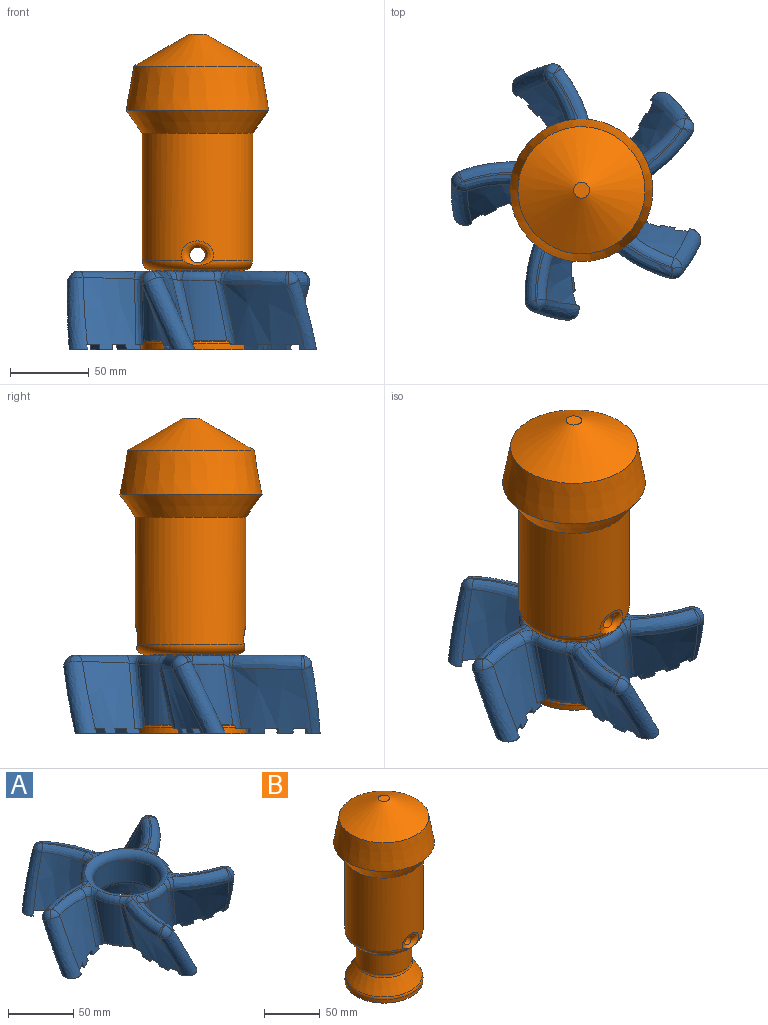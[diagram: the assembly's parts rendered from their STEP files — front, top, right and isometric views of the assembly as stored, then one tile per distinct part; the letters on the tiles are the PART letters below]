
ASSEMBLY  parts=2 mates=1
PART A: 225 faces, bbox 175.2x182.1x61 mm
  f0: plane 42.35x20.28mm, normal (0,0,1), area 71.8mm2, adj f1,f2,f3,f4,f5,f6,f7
  f1: bspline ~10.62x7.36mm, area 56.3mm2, adj f0,f2,f8,f9
  f2: bspline ~43.17x22.23mm, area 274.2mm2, adj f0,f1,f3,f10
  f3: bspline ~8.45x6.28mm, area 40.2mm2, adj f0,f2,f11,f12
  f4: bspline ~9.09x8.11mm, area 21.1mm2, adj f0,f5,f11,f12
  f5: bspline ~56.02x27.79mm, area 540.1mm2, adj f0,f4,f6,f13
  f6: bspline ~8.4x7.98mm, area 34.4mm2, adj f0,f5,f14,f15
  f7: torus R=31.68mm, axis (0,0,-1), area 1732.1mm2, adj f0,f8,f14,f16,f17,f18,f19,f20
  f8: bspline ~9.22x6.2mm, area 33.1mm2, adj f1,f7,f9,f31
  f9: bspline ~52.96x14.35mm, area 308.9mm2, adj f1,f8,f10,f34,f35,f36,f37
  f10: bspline ~61.21x58.82mm, area 1531.5mm2, adj f2,f9,f12,f36,f38,f39,f40,f41
  f11: bspline ~9.17x8.69mm, area 43.6mm2, adj f3,f4,f12
  f12: bspline ~58.82x48.97mm, area 1090.9mm2, adj f3,f4,f10,f11,f13,f38,f46,f47
  f13: bspline ~69.73x58.82mm, area 1849.8mm2, adj f5,f12,f15,f36,f38,f39,f41,f42
  f14: bspline ~9.32x7.99mm, area 39.3mm2, adj f6,f7,f15,f30
  f15: bspline ~52.82x15.4mm, area 214.3mm2, adj f6,f13,f14,f34,f35,f36,f53
  f16: cylinder r=25.33mm len=50.66mm, axis (0,0,-1), area 3136mm2, adj f7,f54
  f17: bspline ~8.62x6.2mm, area 33.1mm2, adj f7,f18,f55,f56
  f18: torus R=28.5mm, axis (0,0,1), area 139.8mm2, adj f7,f17,f19,f57
  f19: bspline ~8.7x7.99mm, area 39.3mm2, adj f7,f18,f58,f59
  f20: plane 45.94x13.84mm, normal (0,0,1), area 71.8mm2, adj f7,f58,f60,f61,f62,f63,f64
  f21: bspline ~8.02x6.42mm, area 33.1mm2, adj f7,f22,f60,f65
  f22: torus R=28.5mm, axis (0,0,1), area 139.8mm2, adj f7,f21,f23,f66
  f23: bspline ~7.99x7.98mm, area 39.3mm2, adj f7,f22,f67,f68
  f24: plane 41.07x26.12mm, normal (0,0,1), area 71.8mm2, adj f7,f68,f69,f70,f71,f72,f73
  f25: bspline ~8.18x6.64mm, area 33.1mm2, adj f7,f26,f72,f74
  f26: torus R=28.5mm, axis (0,0,1), area 139.8mm2, adj f7,f25,f27,f75
  f27: bspline ~8.67x7.99mm, area 39.3mm2, adj f7,f26,f76,f77
  f28: plane 35.99x32.2mm, normal (0,0,1), area 71.8mm2, adj f7,f77,f78,f79,f80,f81,f82
  f29: bspline ~9.15x6.44mm, area 33.1mm2, adj f7,f30,f81,f83
  f30: torus R=28.5mm, axis (0,0,1), area 139.8mm2, adj f7,f14,f29,f53
  f31: torus R=28.5mm, axis (0,0,1), area 139.8mm2, adj f7,f8,f32,f37
  f32: bspline ~9.1x7.81mm, area 39.3mm2, adj f7,f31,f84,f85
  f33: plane 46.31x6.53mm, normal (0,0,1), area 71.8mm2, adj f7,f55,f84,f86,f87,f88,f89
  f34: torus R=30.33mm, axis (0,0,-1), area 364.3mm2, adj f9,f15,f35,f37,f53,f56,f57,f59
  f35: cylinder r=35.33mm len=18.77mm, axis (0,0,-1), area 1.8mm2, adj f9,f15,f34,f36
  f36: plane 18.75x12.96mm, normal (0,0,-1), area 72.9mm2, adj f9,f10,f13,f15,f35,f45
  f37: cylinder r=35mm len=38.6mm, axis (0,0,-1), area 809.9mm2, adj f9,f31,f34,f85
  f38: plane 18.21x15.93mm, normal (0,0,-1), area 134.9mm2, adj f10,f12,f13,f39,f49
  f39: plane 12.49x10.79mm, normal (-0.65,0.76,0), area 55.7mm2, adj f10,f13,f38,f51,f95,f96,f97
  f40: plane 6.58x6.34mm, normal (0,0,1), area 0mm2, adj f10,f97
  f41: plane 12.32x10.63mm, normal (0.65,-0.76,0), area 55.5mm2, adj f10,f13,f42,f51,f95,f96,f97
  f42: plane 17.06x16.85mm, normal (0,0,-1), area 135.3mm2, adj f10,f13,f41,f43
  f43: plane 12.25x10.57mm, normal (-0.65,0.76,0), area 55.8mm2, adj f10,f13,f42,f50,f98,f99,f100
  f44: plane 7.76x4.83mm, normal (0,0,1), area 0mm2, adj f10,f100
  f45: plane 12.29x10.61mm, normal (0.65,-0.76,0), area 56.6mm2, adj f10,f13,f36,f50,f98,f99,f100
  f46: cylinder r=7.5mm len=8.2mm, axis (0,0,-1), area 0.9mm2, adj f12,f52,f101,f102
  f47: cylinder r=7.5mm len=12.48mm, axis (0,0,-1), area 0mm2, adj f12,f48,f49,f102
  f48: plane 12.66x4.02mm, normal (0,0,-1), area 0mm2, adj f12,f47
  f49: plane 12.78x11.04mm, normal (0.65,-0.76,0), area 56.4mm2, adj f12,f13,f38,f47,f52,f101,f102
  f50: cylinder r=100.66mm len=7.6mm, axis (0,0,-1), area 0.9mm2, adj f13,f43,f45,f98
  f51: cylinder r=100.66mm len=6.59mm, axis (0,0,-1), area 0.9mm2, adj f13,f39,f41,f95
  f52: cylinder r=100.66mm len=2.48mm, axis (0,0,-1), area 0.3mm2, adj f13,f46,f49,f101
  f53: cylinder r=35mm len=38.6mm, axis (0,0,-1), area 809.9mm2, adj f15,f30,f34,f83
  f54: torus R=30.33mm, axis (0,0,-1), area 420.4mm2, adj f16,f91
  f55: bspline ~8.93x8.44mm, area 56.3mm2, adj f17,f33,f56,f86
  f56: bspline ~52.96x16.05mm, area 308.9mm2, adj f17,f34,f55,f57,f90,f103,f104
  f57: cylinder r=35mm len=38.6mm, axis (0,0,-1), area 809.9mm2, adj f18,f34,f56,f59
  f58: bspline ~8.62x7.98mm, area 34.4mm2, adj f19,f20,f59,f64
  f59: bspline ~52.82x12.84mm, area 214.3mm2, adj f19,f34,f57,f58,f92,f105,f106
  f60: bspline ~9.43x9.43mm, area 56.3mm2, adj f20,f21,f61,f65
  f61: bspline ~44.92x16.4mm, area 274.2mm2, adj f20,f60,f62,f107
  f62: bspline ~7.22x6.78mm, area 40.2mm2, adj f20,f61,f108,f109
  f63: bspline ~9.07x6.55mm, area 21.1mm2, adj f20,f64,f108,f109
  f64: bspline ~56.54x22.87mm, area 540.1mm2, adj f20,f58,f63,f106
  f65: bspline ~52.96x17.22mm, area 308.9mm2, adj f21,f34,f60,f66,f92,f105,f107
  f66: cylinder r=35mm len=38.6mm, axis (0,0,-1), area 809.9mm2, adj f22,f34,f65,f67
  f67: bspline ~52.82x15.21mm, area 214.3mm2, adj f23,f34,f66,f68,f93,f110,f111
  f68: bspline ~8.97x7.98mm, area 34.4mm2, adj f23,f24,f67,f71
  f69: bspline ~7.29x6.91mm, area 40.2mm2, adj f24,f73,f112,f113
  f70: bspline ~9.07x6.55mm, area 21.1mm2, adj f24,f71,f112,f113
  f71: bspline ~51.4x37.99mm, area 540.1mm2, adj f24,f68,f70,f111
  f72: bspline ~9.51x8.59mm, area 56.3mm2, adj f24,f25,f73,f74
  f73: bspline ~41.2x28.55mm, area 274.2mm2, adj f24,f69,f72,f114
  f74: bspline ~52.96x16.7mm, area 308.9mm2, adj f25,f34,f72,f75,f93,f110,f114
  f75: cylinder r=35mm len=38.6mm, axis (0,0,-1), area 809.9mm2, adj f26,f34,f74,f76
  f76: bspline ~52.82x16.09mm, area 214.3mm2, adj f27,f34,f75,f77,f94,f115,f116
  f77: bspline ~8.49x8.43mm, area 34.4mm2, adj f27,f28,f76,f80
  f78: bspline ~7.83x6.78mm, area 40.2mm2, adj f28,f82,f117,f118
  f79: bspline ~9.07x6.39mm, area 21.1mm2, adj f28,f80,f117,f118
  f80: bspline ~49.43x41.63mm, area 540.1mm2, adj f28,f77,f79,f116
  f81: bspline ~9.75x7.17mm, area 56.3mm2, adj f28,f29,f82,f83
  f82: bspline ~31.37x29.68mm, area 274.2mm2, adj f28,f78,f81,f119
  f83: bspline ~52.96x14.55mm, area 308.9mm2, adj f29,f34,f53,f81,f94,f115,f119
  f84: bspline ~8.24x7.98mm, area 34.4mm2, adj f32,f33,f85,f89
  f85: bspline ~52.82x13.2mm, area 214.3mm2, adj f32,f34,f37,f84,f90,f103,f120
  f86: bspline ~46.04x10.7mm, area 274.2mm2, adj f33,f55,f87,f104
  f87: bspline ~8.23x6.31mm, area 40.2mm2, adj f33,f86,f121,f122
  f88: bspline ~9.47x9.09mm, area 21.1mm2, adj f33,f89,f121,f122
  f89: bspline ~58.82x14.67mm, area 540.1mm2, adj f33,f84,f88,f120
  f90: cylinder r=35.33mm len=19.52mm, axis (0,0,-1), area 1.8mm2, adj f34,f56,f85,f103
  f91: cone r=34.66mm half-angle=30deg, axis (0,0,-1), area 3300.8mm2, adj f34,f54
  f92: cylinder r=35.33mm len=18.35mm, axis (0,0,-1), area 1.8mm2, adj f34,f59,f65,f105
  f93: cylinder r=35.33mm len=15.39mm, axis (0,0,-1), area 1.8mm2, adj f34,f67,f74,f110
  f94: cylinder r=35.33mm len=16.19mm, axis (0,0,-1), area 1.8mm2, adj f34,f76,f83,f115
  f95: plane 17.71x16.43mm, normal (0,0,-1), area 136.6mm2, adj f39,f41,f51,f96
  f96: bspline ~56.9x34.03mm, area 1mm2, adj f39,f41,f95,f97
  f97: cylinder r=85.66mm len=6.54mm, axis (0,0,-1), area 0mm2, adj f39,f40,f41,f96
  f98: plane 17.6x16.4mm, normal (0,0,-1), area 136.7mm2, adj f43,f45,f50,f99
  f99: bspline ~56.9x34.03mm, area 0.9mm2, adj f43,f45,f98,f100
  f100: cylinder r=85.66mm len=7.74mm, axis (0,0,-1), area 0mm2, adj f43,f44,f45,f99
  f101: plane 14.53x13.46mm, normal (0,0,-1), area 111.7mm2, adj f46,f49,f52,f102
  f102: bspline ~34.67x29.41mm, area 1.6mm2, adj f46,f47,f49,f101
  f103: plane 19.5x8.87mm, normal (0,0,-1), area 72.9mm2, adj f56,f85,f90,f104,f120,f123
  f104: bspline ~61.2x58.82mm, area 1531.5mm2, adj f56,f86,f103,f122,f123,f124,f125,f126
  f105: plane 18.34x10.86mm, normal (0,0,-1), area 57.6mm2, adj f59,f65,f92,f106,f107,f131
  f106: bspline ~75.44x58.82mm, area 1851.2mm2, adj f59,f64,f105,f109,f131,f132,f133,f134
  f107: bspline ~59.81x58.82mm, area 1532.7mm2, adj f61,f65,f105,f109,f131,f132,f133,f135
  f108: bspline ~8.9x8.69mm, area 65.3mm2, adj f62,f63,f109
  f109: bspline ~58.82x46.45mm, area 1090.9mm2, adj f62,f63,f106,f107,f108,f147,f148,f149
  f110: plane 18.33x14.91mm, normal (0,0,-1), area 72.9mm2, adj f67,f74,f93,f111,f114,f156
  f111: bspline ~70.76x58.82mm, area 1849.8mm2, adj f67,f71,f110,f113,f156,f157,f158,f159
  f112: bspline ~8.69x7.43mm, area 47mm2, adj f69,f70,f113
  f113: bspline ~58.82x42.6mm, area 1090.9mm2, adj f69,f70,f111,f112,f114,f163,f164,f166
  f114: bspline ~58.82x57.24mm, area 1531.5mm2, adj f73,f74,f110,f113,f156,f158,f159,f160
  f115: plane 17.51x16.45mm, normal (0,0,-1), area 72.9mm2, adj f76,f83,f94,f116,f119,f171
  f116: bspline ~62.06x59.15mm, area 1849.8mm2, adj f76,f80,f115,f118,f171,f172,f173,f174
  f117: bspline ~8.69x7.94mm, area 42.7mm2, adj f78,f79,f118
  f118: bspline ~58.82x43.56mm, area 1090.9mm2, adj f78,f79,f116,f117,f119,f178,f179,f181
  f119: bspline ~58.82x55.76mm, area 1531.5mm2, adj f82,f83,f115,f118,f171,f173,f174,f175
  f120: bspline ~73.54x58.82mm, area 1849.8mm2, adj f85,f89,f103,f122,f123,f124,f125,f127
  f121: bspline ~9.5x8.69mm, area 52.2mm2, adj f87,f88,f122
  f122: bspline ~58.82x49.59mm, area 1090.9mm2, adj f87,f88,f104,f120,f121,f124,f188,f190
  f123: plane 14.96x6.29mm, normal (0.92,0.39,0), area 56.6mm2, adj f103,f104,f120,f186,f193,f194,f195
  f124: plane 18.53x13.68mm, normal (0,0,-1), area 134.9mm2, adj f104,f120,f122,f125,f188
  f125: plane 15.21x6.4mm, normal (-0.92,-0.39,0), area 55.7mm2, adj f104,f120,f124,f187,f196,f197,f198
  f126: plane 8.2x4.02mm, normal (0,0,1), area 0mm2, adj f104,f198
  f127: plane 15x6.31mm, normal (0.92,0.39,0), area 55.5mm2, adj f104,f120,f128,f187,f196,f197,f198
  f128: plane 16.84x14.38mm, normal (0,0,-1), area 135.3mm2, adj f104,f120,f127,f129
  f129: plane 14.91x6.27mm, normal (-0.92,-0.39,0), area 55.8mm2, adj f104,f120,f128,f186,f193,f194,f195
  f130: plane 8.87x2.21mm, normal (0,0,1), area 0mm2, adj f104,f193
  f131: cylinder r=1mm len=15.41mm, axis (-1,-0.08,0), area 24.1mm2, adj f105,f106,f107,f132
  f132: plane 15.68x1.7mm, normal (-0.08,1,0), area 26mm2, adj f106,f107,f131,f133
  f133: cylinder r=1mm len=15.43mm, axis (-1,-0.08,0), area 24mm2, adj f106,f107,f132,f134,f199,f200,f201
  f134: cylinder r=100.66mm len=7.93mm, axis (0,0,-1), area 0.7mm2, adj f106,f133,f135,f201
  f135: cylinder r=1mm len=15.5mm, axis (1,0.08,0), area 23.7mm2, adj f106,f107,f134,f136,f199,f200,f201
  f136: plane 15.53x1.7mm, normal (0.08,-1,0), area 25.6mm2, adj f106,f107,f135,f137
  f137: cylinder r=1mm len=15.52mm, axis (1,0.08,0), area 23.7mm2, adj f106,f107,f136,f138
  f138: plane 15.14x8.29mm, normal (0,0,-1), area 105.2mm2, adj f106,f107,f137,f139
  f139: cylinder r=1mm len=15.35mm, axis (-1,-0.08,0), area 23.6mm2, adj f106,f107,f138,f140
  f140: plane 15.53x1.7mm, normal (-0.08,1,0), area 25.5mm2, adj f106,f107,f139,f141
  f141: cylinder r=1mm len=15.38mm, axis (-1,-0.08,0), area 23.6mm2, adj f106,f107,f140,f142,f202,f203,f204
  f142: cylinder r=100.66mm len=7.88mm, axis (0,0,-1), area 0.7mm2, adj f106,f141,f143,f204
  f143: cylinder r=1mm len=15.39mm, axis (1,0.08,0), area 23.7mm2, adj f106,f107,f142,f144,f151,f202,f203,f204
  f144: plane 15.67x1.7mm, normal (0.08,-1,0), area 25.6mm2, adj f106,f107,f143,f145
  f145: cylinder r=1mm len=15.39mm, axis (1,0.08,0), area 23.7mm2, adj f106,f107,f144,f146
  f146: plane 16.6x8.11mm, normal (0,0,-1), area 104.6mm2, adj f106,f107,f145,f147
  f147: cylinder r=1mm len=15.87mm, axis (-1,-0.08,0), area 23.9mm2, adj f106,f107,f109,f146,f148
  f148: plane 15.95x1.7mm, normal (-0.08,1,0), area 25.9mm2, adj f106,f109,f147,f149
  f149: cylinder r=1mm len=15.89mm, axis (-1,-0.08,0), area 24mm2, adj f106,f109,f148,f150,f154,f155,f205,f206
  f150: cylinder r=100.66mm len=2.46mm, axis (0,0,-1), area 0.2mm2, adj f106,f149,f153,f206
  f151: plane 7.9x1.13mm, normal (0,0,1), area 0mm2, adj f107,f143,f202
  f152: plane 7.97x0.6mm, normal (0,0,1), area 0mm2, adj f107,f199
  f153: cylinder r=7.5mm len=6.32mm, axis (0,0,-1), area 0.9mm2, adj f109,f150,f205,f206
  f154: cylinder r=7.5mm len=9.05mm, axis (0,0,-1), area 0mm2, adj f109,f149,f155,f205
  f155: plane 9.23x8.56mm, normal (0,0,-1), area 0mm2, adj f109,f149,f154
  f156: plane 15.8x3.71mm, normal (-0.97,0.23,0), area 56.6mm2, adj f110,f111,f114,f157,f207,f208,f209
  f157: cylinder r=100.66mm len=8.49mm, axis (0,0,-1), area 0.9mm2, adj f111,f156,f158,f209
  f158: plane 15.75x3.7mm, normal (0.97,-0.23,0), area 55.8mm2, adj f111,f114,f157,f159,f207,f208,f209
  f159: plane 17.3x12.09mm, normal (0,0,-1), area 135.3mm2, adj f111,f114,f158,f160
  f160: plane 15.84x3.72mm, normal (-0.97,0.23,0), area 55.5mm2, adj f111,f114,f159,f161,f210,f211,f212
  f161: cylinder r=100.66mm len=8.93mm, axis (0,0,-1), area 0.9mm2, adj f111,f160,f162,f212
  f162: plane 16.07x3.77mm, normal (0.97,-0.23,0), area 55.7mm2, adj f111,f114,f161,f163,f210,f211,f212
  f163: plane 15.69x12.44mm, normal (0,0,-1), area 134.9mm2, adj f111,f113,f114,f162,f164
  f164: plane 16.44x3.86mm, normal (-0.97,0.23,0), area 56.4mm2, adj f111,f113,f163,f165,f167,f213,f214
  f165: cylinder r=100.66mm len=3.14mm, axis (0,0,-1), area 0.3mm2, adj f111,f164,f166,f214
  f166: cylinder r=7.5mm len=6.95mm, axis (0,0,-1), area 0.9mm2, adj f113,f165,f213,f214
  f167: cylinder r=7.5mm len=10.64mm, axis (0,0,-1), area 0mm2, adj f113,f164,f168,f213
  f168: plane 10.82x7.46mm, normal (0,0,-1), area 0mm2, adj f113,f167
  f169: plane 8.98x1.62mm, normal (0,0,1), area 0mm2, adj f114,f210
  f170: plane 8.46x3.46mm, normal (0,0,1), area 0mm2, adj f114,f207
  f171: plane 13.88x8.41mm, normal (-0.52,-0.86,0), area 56.6mm2, adj f115,f116,f119,f172,f215,f216,f217
  f172: cylinder r=100.66mm len=7.08mm, axis (0,0,-1), area 0.9mm2, adj f116,f171,f173,f217
  f173: plane 13.84x8.38mm, normal (0.52,0.86,0), area 55.8mm2, adj f116,f119,f172,f174,f215,f216,f217
  f174: plane 18.06x15.21mm, normal (0,0,-1), area 135.3mm2, adj f116,f119,f173,f175
  f175: plane 13.92x8.43mm, normal (-0.52,-0.86,0), area 55.5mm2, adj f116,f119,f174,f176,f218,f219,f220
  f176: cylinder r=100.66mm len=7.98mm, axis (0,0,-1), area 0.9mm2, adj f116,f175,f177,f220
  f177: plane 14.12x8.55mm, normal (0.52,0.86,0), area 55.7mm2, adj f116,f119,f176,f178,f218,f219,f220
  f178: plane 16.62x16.11mm, normal (0,0,-1), area 134.9mm2, adj f116,f118,f119,f177,f179
  f179: plane 14.44x8.75mm, normal (-0.52,-0.86,0), area 56.4mm2, adj f116,f118,f178,f180,f182,f221,f222
  f180: cylinder r=100.66mm len=2.95mm, axis (0,0,-1), area 0.3mm2, adj f116,f179,f181,f222
  f181: cylinder r=7.5mm len=7.97mm, axis (0,0,-1), area 0.9mm2, adj f118,f180,f221,f222
  f182: cylinder r=7.5mm len=12.15mm, axis (0,0,-1), area 0mm2, adj f118,f179,f183,f221
  f183: plane 12.33x5.15mm, normal (0,0,-1), area 0mm2, adj f118,f182
  f184: plane 8.05x4.31mm, normal (0,0,1), area 0mm2, adj f119,f218
  f185: plane 6.99x5.9mm, normal (0,0,1), area 0mm2, adj f119,f215
  f186: cylinder r=100.66mm len=8.76mm, axis (0,0,-1), area 0.9mm2, adj f120,f123,f129,f195
  f187: cylinder r=100.66mm len=8.19mm, axis (0,0,-1), area 0.9mm2, adj f120,f125,f127,f196
  f188: plane 15.57x6.55mm, normal (0.92,0.39,0), area 56.4mm2, adj f120,f122,f124,f189,f191,f223,f224
  f189: cylinder r=100.66mm len=2.6mm, axis (0,0,-1), area 0.3mm2, adj f120,f188,f190,f224
  f190: cylinder r=7.5mm len=7.63mm, axis (0,0,-1), area 0.9mm2, adj f122,f189,f223,f224
  f191: cylinder r=7.5mm len=11.58mm, axis (0,0,-1), area 0mm2, adj f122,f188,f192,f223
  f192: plane 11.77x6.21mm, normal (0,0,-1), area 0mm2, adj f122,f191
  f193: cylinder r=85.66mm len=8.85mm, axis (0,0,-1), area 0mm2, adj f123,f129,f130,f194
  f194: bspline ~60.48x29.41mm, area 0.9mm2, adj f123,f129,f193,f195
  f195: plane 16.3x14.7mm, normal (0,0,-1), area 136.7mm2, adj f123,f129,f186,f194
  f196: plane 17.86x14.05mm, normal (0,0,-1), area 136.6mm2, adj f125,f127,f187,f197
  f197: bspline ~60.48x29.41mm, area 1mm2, adj f125,f127,f196,f198
  f198: cylinder r=85.66mm len=8.16mm, axis (0,0,-1), area 0mm2, adj f125,f126,f127,f197
  f199: cylinder r=85.66mm len=7.95mm, axis (0,0,-1), area 0mm2, adj f133,f135,f152,f200
  f200: bspline ~59.66x29.41mm, area 0.8mm2, adj f133,f135,f199,f201
  f201: plane 15.57x8.33mm, normal (0,0,-1), area 106.3mm2, adj f133,f134,f135,f200
  f202: cylinder r=85.66mm len=7.87mm, axis (0,0,-1), area 0mm2, adj f141,f143,f151,f203
  f203: bspline ~59.66x29.41mm, area 0.8mm2, adj f141,f143,f202,f204
  f204: plane 15.98x8.29mm, normal (0,0,-1), area 106.4mm2, adj f141,f142,f143,f203
  f205: bspline ~32.55x29.41mm, area 1.5mm2, adj f149,f153,f154,f206
  f206: plane 15.32x8.63mm, normal (0,0,-1), area 96.4mm2, adj f149,f150,f153,f205
  f207: cylinder r=85.66mm len=8.44mm, axis (0,0,-1), area 0mm2, adj f156,f158,f170,f208
  f208: bspline ~56.24x33.93mm, area 0.9mm2, adj f156,f158,f207,f209
  f209: plane 18.13x11.94mm, normal (0,0,-1), area 136.7mm2, adj f156,f157,f158,f208
  f210: cylinder r=85.66mm len=8.94mm, axis (0,0,-1), area 0mm2, adj f160,f162,f169,f211
  f211: bspline ~56.24x33.93mm, area 1mm2, adj f160,f162,f210,f212
  f212: plane 16.32x12.4mm, normal (0,0,-1), area 136.6mm2, adj f160,f161,f162,f211
  f213: bspline ~29.84x29.41mm, area 1.6mm2, adj f164,f166,f167,f214
  f214: plane 15.04x10.79mm, normal (0,0,-1), area 111.7mm2, adj f164,f165,f166,f213
  f215: cylinder r=85.66mm len=6.96mm, axis (0,0,-1), area 0mm2, adj f171,f173,f185,f216
  f216: bspline ~47.75x47.46mm, area 0.9mm2, adj f171,f173,f215,f217
  f217: plane 18.79x14.9mm, normal (0,0,-1), area 136.7mm2, adj f171,f172,f173,f216
  f218: cylinder r=85.66mm len=8.02mm, axis (0,0,-1), area 0mm2, adj f175,f177,f184,f219
  f219: bspline ~47.75x47.46mm, area 1mm2, adj f175,f177,f218,f220
  f220: plane 17.22x15.83mm, normal (0,0,-1), area 136.6mm2, adj f175,f176,f177,f219
  f221: bspline ~30.61x30.28mm, area 1.6mm2, adj f179,f181,f182,f222
  f222: plane 14.6x12.93mm, normal (0,0,-1), area 111.7mm2, adj f179,f180,f181,f221
  f223: bspline ~35.34x29.41mm, area 1.6mm2, adj f188,f190,f191,f224
  f224: plane 15.45x11.74mm, normal (0,0,-1), area 111.7mm2, adj f188,f189,f190,f223
PART B: 16 faces, bbox 90.4x90.4x200 mm
  f0: cylinder r=35mm len=80.51mm, axis (0,0,-1), area 17279mm2, adj f1,f13,f14,f15
  f1: cone r=35mm half-angle=35deg, axis (0,0,1), area 4474.6mm2, adj f0,f2
  f2: cone r=45.19mm half-angle=10deg, axis (0,0,-1), area 7615.8mm2, adj f1,f3
  f3: cone r=40.26mm half-angle=60deg, axis (0,0,-1), area 5789.6mm2, adj f2,f4
  f4: plane 10x10mm, normal (0,0,1), area 78.5mm2, adj f3
  f5: cylinder r=35mm len=70mm, axis (0,0,-1), area 813.1mm2, adj f6,f11
  f6: torus R=30mm, axis (0,0,-1), area 572mm2, adj f5,f7
  f7: cone r=34.33mm half-angle=30deg, axis (0,0,-1), area 3264.8mm2, adj f6,f8
  f8: torus R=30mm, axis (0,0,-1), area 414.9mm2, adj f7,f9
  f9: cylinder r=25mm len=50mm, axis (0,0,-1), area 3384.5mm2, adj f8,f10
  f10: torus R=30mm, axis (0,0,-1), area 1201.4mm2, adj f9,f15
  f11: plane 70x70mm, normal (0,0,-1), area 3848.5mm2, adj f5
  f12: cylinder r=5mm len=62mm, axis (0,-1,0), area 1906.1mm2, adj f13,f14
  f13: bspline ~20.3x17.99mm, area 262.8mm2, adj f0,f12,f15
  f14: bspline ~20.3x17.99mm, area 253.3mm2, adj f0,f12,f15
  f15: torus R=28.5mm, axis (0,0,1), area 1864.6mm2, adj f0,f10,f13,f14
PLACE A rot(axis=(0,0,-1),0.2deg) t=(0,0,-0.02)mm
PLACE B t=(0,0,0.07)mm fixed
MATE revolute B.f0 <-> A.f7  axis (0,0,-1) through (0,0,6.26)mm
